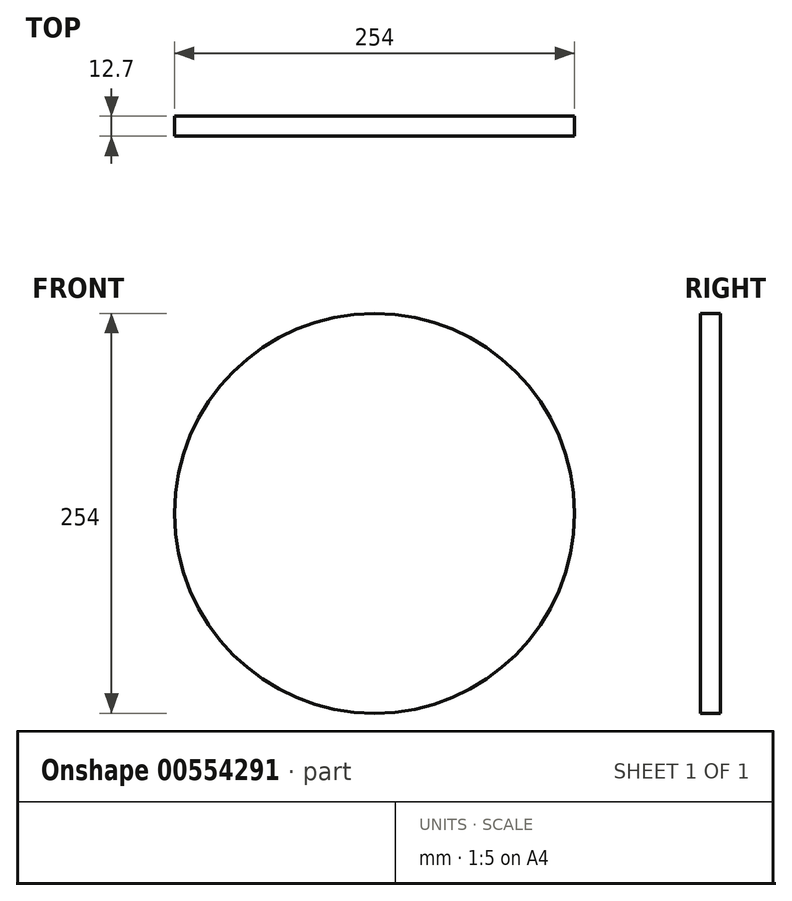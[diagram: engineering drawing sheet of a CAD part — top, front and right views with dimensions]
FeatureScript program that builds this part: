
annotation { "Feature Type Name" : "Feature", "Feature Type Description" : "" }
export const myFeature = defineFeature(function(context is Context, id is Id, definition is map)
    precondition{}
    {
        {
            var Q0;
            Q0=qCreatedBy(makeId("Front.planeOp"),FACE);
            var sketch = newSketch(context, id + "F0", { "sketchPlane" : qUnion([Q0])});
            skCircle(sketch, "E0", {"center": v(0, 0) * mm, "radius": 127 * mm});
            skSolve(sketch);
        }
        {
            var Q0;
            Q0 = qSketchRegion(id + "F0", true);
            extrude(context, id + "F1", {"entities" : qUnion([Q0]), "depth" : 12.7 * mm, "offsetDistance" : 25.4 * mm});
        }
    });
